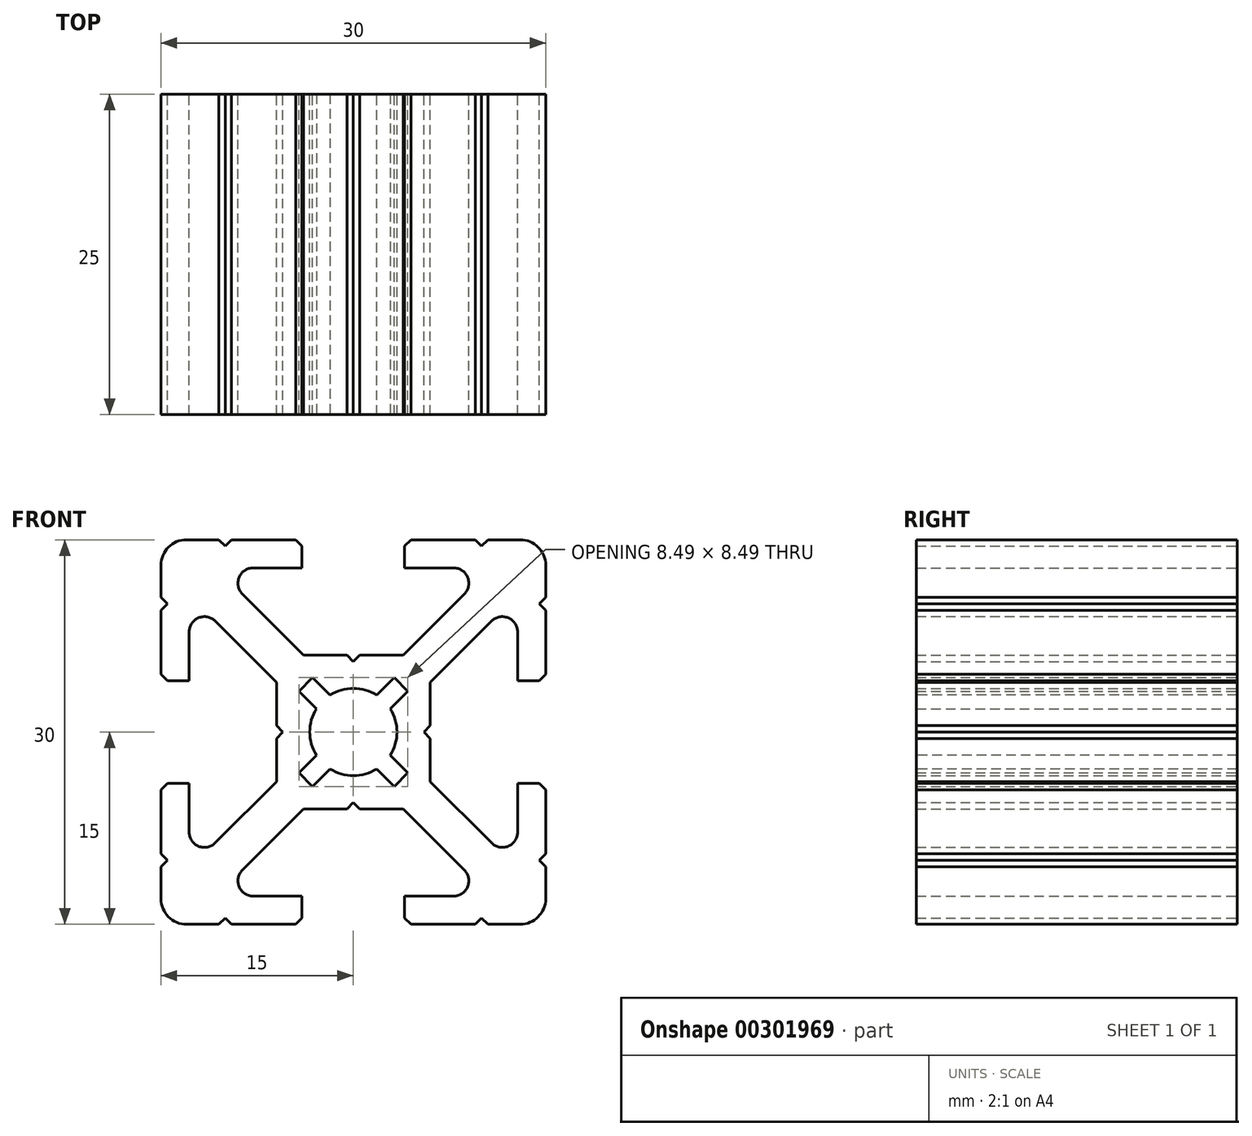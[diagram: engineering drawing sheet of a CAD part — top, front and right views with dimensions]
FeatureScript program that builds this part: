
annotation { "Feature Type Name" : "Feature", "Feature Type Description" : "" }
export const myFeature = defineFeature(function(context is Context, id is Id, definition is map)
    precondition{}
    {
        {
            var Q0;
            Q0=qCreatedBy(makeId("Front.planeOp"),FACE);
            var sketch = newSketch(context, id + "F0", { "sketchPlane" : qUnion([Q0])});
            skLineSegment(sketch, "E0", {"start": v(-2.88, -1.81) * mm, "end": v(-4.24, -3.18) * mm});
            skLineSegment(sketch, "E1", {"start": v(-4.24, -3.18) * mm, "end": v(-3.18, -4.24) * mm});
            skLineSegment(sketch, "E2", {"start": v(-3.18, -4.24) * mm, "end": v(-1.81, -2.88) * mm});
            skLineSegment(sketch, "E3", {"start": v(-1.81, -2.88) * mm, "end": v(-1.81, -2.88) * mm});
            skArc(sketch, "E4", {"start": v(-1.81, -2.88) * mm, "mid": v(0, -3.4) * mm, "end": v(1.81, -2.88) * mm});
            skLineSegment(sketch, "E5", {"start": v(1.81, -2.88) * mm, "end": v(1.81, -2.88) * mm});
            skLineSegment(sketch, "E6", {"start": v(1.81, -2.88) * mm, "end": v(3.18, -4.24) * mm});
            skLineSegment(sketch, "E7", {"start": v(3.18, -4.24) * mm, "end": v(4.24, -3.18) * mm});
            skLineSegment(sketch, "E8", {"start": v(4.24, -3.18) * mm, "end": v(2.88, -1.81) * mm});
            skLineSegment(sketch, "E9", {"start": v(2.88, -1.81) * mm, "end": v(2.88, -1.81) * mm});
            skArc(sketch, "E10", {"start": v(2.88, -1.81) * mm, "mid": v(3.4, 0) * mm, "end": v(2.88, 1.81) * mm});
            skLineSegment(sketch, "E11", {"start": v(2.88, 1.81) * mm, "end": v(2.88, 1.81) * mm});
            skLineSegment(sketch, "E12", {"start": v(2.88, 1.81) * mm, "end": v(4.24, 3.18) * mm});
            skLineSegment(sketch, "E13", {"start": v(4.24, 3.18) * mm, "end": v(3.18, 4.24) * mm});
            skLineSegment(sketch, "E14", {"start": v(3.18, 4.24) * mm, "end": v(1.81, 2.88) * mm});
            skLineSegment(sketch, "E15", {"start": v(1.81, 2.88) * mm, "end": v(1.81, 2.88) * mm});
            skArc(sketch, "E16", {"start": v(1.81, 2.88) * mm, "mid": v(0, 3.4) * mm, "end": v(-1.81, 2.88) * mm});
            skLineSegment(sketch, "E17", {"start": v(-1.81, 2.88) * mm, "end": v(-1.81, 2.88) * mm});
            skLineSegment(sketch, "E18", {"start": v(-1.81, 2.88) * mm, "end": v(-3.18, 4.24) * mm});
            skLineSegment(sketch, "E19", {"start": v(-3.18, 4.24) * mm, "end": v(-4.24, 3.18) * mm});
            skLineSegment(sketch, "E20", {"start": v(-4.24, 3.18) * mm, "end": v(-2.88, 1.81) * mm});
            skLineSegment(sketch, "E21", {"start": v(-2.88, 1.81) * mm, "end": v(-2.88, 1.81) * mm});
            skArc(sketch, "E22", {"start": v(-2.88, 1.81) * mm, "mid": v(-3.4, 0) * mm, "end": v(-2.88, -1.81) * mm});
            skArc(sketch, "E23", {"start": v(-10.77, 8.65) * mm, "mid": v(-11.38, 8.98) * mm, "end": v(-12.07, 8.9) * mm});
            skArc(sketch, "E24", {"start": v(-12.07, 8.9) * mm, "mid": v(-12.6, 8.47) * mm, "end": v(-12.8, 7.81) * mm});
            skLineSegment(sketch, "E25", {"start": v(-12.8, 7.81) * mm, "end": v(-12.8, 4) * mm});
            skLineSegment(sketch, "E26", {"start": v(-12.8, 4) * mm, "end": v(-14.5, 4) * mm});
            skLineSegment(sketch, "E27", {"start": v(-14.5, 4) * mm, "end": v(-15, 4.5) * mm});
            skLineSegment(sketch, "E28", {"start": v(-15, 4.5) * mm, "end": v(-15, 9.5) * mm});
            skLineSegment(sketch, "E29", {"start": v(-15, 9.5) * mm, "end": v(-14.5, 10) * mm});
            skLineSegment(sketch, "E30", {"start": v(-14.5, 10) * mm, "end": v(-15, 10.5) * mm});
            skLineSegment(sketch, "E31", {"start": v(-15, 10.5) * mm, "end": v(-15, 13) * mm});
            skLineSegment(sketch, "E32", {"start": v(-15, 13) * mm, "end": v(-15, 13) * mm});
            skArc(sketch, "E33", {"start": v(-13, 15) * mm, "mid": v(-14.41, 14.41) * mm, "end": v(-15, 13) * mm});
            skLineSegment(sketch, "E34", {"start": v(-13, 15) * mm, "end": v(-13, 15) * mm});
            skLineSegment(sketch, "E35", {"start": v(-13, 15) * mm, "end": v(-10.5, 15) * mm});
            skLineSegment(sketch, "E36", {"start": v(-10.5, 15) * mm, "end": v(-10, 14.5) * mm});
            skLineSegment(sketch, "E37", {"start": v(-10, 14.5) * mm, "end": v(-9.5, 15) * mm});
            skLineSegment(sketch, "E38", {"start": v(-9.5, 15) * mm, "end": v(-4.5, 15) * mm});
            skLineSegment(sketch, "E39", {"start": v(-4.5, 15) * mm, "end": v(-4, 14.5) * mm});
            skLineSegment(sketch, "E40", {"start": v(-4, 14.5) * mm, "end": v(-4, 12.8) * mm});
            skLineSegment(sketch, "E41", {"start": v(-4, 12.8) * mm, "end": v(-7.81, 12.8) * mm});
            skArc(sketch, "E42", {"start": v(-7.81, 12.8) * mm, "mid": v(-8.47, 12.6) * mm, "end": v(-8.9, 12.07) * mm});
            skArc(sketch, "E43", {"start": v(-8.9, 12.07) * mm, "mid": v(-8.98, 11.38) * mm, "end": v(-8.65, 10.77) * mm});
            skLineSegment(sketch, "E44", {"start": v(-8.65, 10.77) * mm, "end": v(-3.88, 6) * mm});
            skLineSegment(sketch, "E45", {"start": v(-3.88, 6) * mm, "end": v(-0.5, 6) * mm});
            skLineSegment(sketch, "E46", {"start": v(-0.5, 6) * mm, "end": v(0, 5.5) * mm});
            skLineSegment(sketch, "E47", {"start": v(0, 5.5) * mm, "end": v(0.5, 6) * mm});
            skLineSegment(sketch, "E48", {"start": v(0.5, 6) * mm, "end": v(3.88, 6) * mm});
            skLineSegment(sketch, "E49", {"start": v(3.88, 6) * mm, "end": v(8.65, 10.77) * mm});
            skArc(sketch, "E50", {"start": v(8.65, 10.77) * mm, "mid": v(8.98, 11.38) * mm, "end": v(8.9, 12.07) * mm});
            skArc(sketch, "E51", {"start": v(8.9, 12.07) * mm, "mid": v(8.47, 12.6) * mm, "end": v(7.81, 12.8) * mm});
            skLineSegment(sketch, "E52", {"start": v(7.81, 12.8) * mm, "end": v(4, 12.8) * mm});
            skLineSegment(sketch, "E53", {"start": v(4, 12.8) * mm, "end": v(4, 14.5) * mm});
            skLineSegment(sketch, "E54", {"start": v(4, 14.5) * mm, "end": v(4.5, 15) * mm});
            skLineSegment(sketch, "E55", {"start": v(4.5, 15) * mm, "end": v(9.5, 15) * mm});
            skLineSegment(sketch, "E56", {"start": v(9.5, 15) * mm, "end": v(10, 14.5) * mm});
            skLineSegment(sketch, "E57", {"start": v(10, 14.5) * mm, "end": v(10.5, 15) * mm});
            skLineSegment(sketch, "E58", {"start": v(10.5, 15) * mm, "end": v(13, 15) * mm});
            skLineSegment(sketch, "E59", {"start": v(13, 15) * mm, "end": v(13, 15) * mm});
            skArc(sketch, "E60", {"start": v(15, 13) * mm, "mid": v(14.41, 14.41) * mm, "end": v(13, 15) * mm});
            skLineSegment(sketch, "E61", {"start": v(15, 13) * mm, "end": v(15, 13) * mm});
            skLineSegment(sketch, "E62", {"start": v(15, 13) * mm, "end": v(15, 10.5) * mm});
            skLineSegment(sketch, "E63", {"start": v(15, 10.5) * mm, "end": v(14.5, 10) * mm});
            skLineSegment(sketch, "E64", {"start": v(14.5, 10) * mm, "end": v(15, 9.5) * mm});
            skLineSegment(sketch, "E65", {"start": v(15, 9.5) * mm, "end": v(15, 4.5) * mm});
            skLineSegment(sketch, "E66", {"start": v(15, 4.5) * mm, "end": v(14.5, 4) * mm});
            skLineSegment(sketch, "E67", {"start": v(14.5, 4) * mm, "end": v(12.8, 4) * mm});
            skLineSegment(sketch, "E68", {"start": v(12.8, 4) * mm, "end": v(12.8, 7.81) * mm});
            skArc(sketch, "E69", {"start": v(12.8, 7.81) * mm, "mid": v(12.6, 8.47) * mm, "end": v(12.07, 8.9) * mm});
            skArc(sketch, "E70", {"start": v(12.07, 8.9) * mm, "mid": v(11.38, 8.98) * mm, "end": v(10.77, 8.65) * mm});
            skLineSegment(sketch, "E71", {"start": v(10.77, 8.65) * mm, "end": v(10.77, 8.65) * mm});
            skLineSegment(sketch, "E72", {"start": v(10.77, 8.65) * mm, "end": v(6, 3.88) * mm});
            skLineSegment(sketch, "E73", {"start": v(6, 3.88) * mm, "end": v(6, 0.5) * mm});
            skLineSegment(sketch, "E74", {"start": v(6, 0.5) * mm, "end": v(5.5, 0) * mm});
            skLineSegment(sketch, "E75", {"start": v(5.5, 0) * mm, "end": v(6, -0.5) * mm});
            skLineSegment(sketch, "E76", {"start": v(6, -0.5) * mm, "end": v(6, -3.88) * mm});
            skLineSegment(sketch, "E77", {"start": v(6, -3.88) * mm, "end": v(10.77, -8.65) * mm});
            skLineSegment(sketch, "E78", {"start": v(10.77, -8.65) * mm, "end": v(10.77, -8.65) * mm});
            skArc(sketch, "E79", {"start": v(10.77, -8.65) * mm, "mid": v(11.38, -8.98) * mm, "end": v(12.07, -8.9) * mm});
            skArc(sketch, "E80", {"start": v(12.07, -8.9) * mm, "mid": v(12.6, -8.47) * mm, "end": v(12.8, -7.81) * mm});
            skLineSegment(sketch, "E81", {"start": v(12.8, -7.81) * mm, "end": v(12.8, -4) * mm});
            skLineSegment(sketch, "E82", {"start": v(12.8, -4) * mm, "end": v(14.5, -4) * mm});
            skLineSegment(sketch, "E83", {"start": v(14.5, -4) * mm, "end": v(15, -4.5) * mm});
            skLineSegment(sketch, "E84", {"start": v(15, -4.5) * mm, "end": v(15, -9.5) * mm});
            skLineSegment(sketch, "E85", {"start": v(15, -9.5) * mm, "end": v(14.5, -10) * mm});
            skLineSegment(sketch, "E86", {"start": v(14.5, -10) * mm, "end": v(15, -10.5) * mm});
            skLineSegment(sketch, "E87", {"start": v(15, -10.5) * mm, "end": v(15, -13) * mm});
            skLineSegment(sketch, "E88", {"start": v(15, -13) * mm, "end": v(15, -13) * mm});
            skArc(sketch, "E89", {"start": v(13, -15) * mm, "mid": v(14.41, -14.41) * mm, "end": v(15, -13) * mm});
            skLineSegment(sketch, "E90", {"start": v(13, -15) * mm, "end": v(13, -15) * mm});
            skLineSegment(sketch, "E91", {"start": v(13, -15) * mm, "end": v(10.5, -15) * mm});
            skLineSegment(sketch, "E92", {"start": v(10.5, -15) * mm, "end": v(10, -14.5) * mm});
            skLineSegment(sketch, "E93", {"start": v(10, -14.5) * mm, "end": v(9.5, -15) * mm});
            skLineSegment(sketch, "E94", {"start": v(9.5, -15) * mm, "end": v(4.5, -15) * mm});
            skLineSegment(sketch, "E95", {"start": v(4.5, -15) * mm, "end": v(4, -14.5) * mm});
            skLineSegment(sketch, "E96", {"start": v(4, -14.5) * mm, "end": v(4, -12.8) * mm});
            skLineSegment(sketch, "E97", {"start": v(4, -12.8) * mm, "end": v(7.81, -12.8) * mm});
            skArc(sketch, "E98", {"start": v(7.81, -12.8) * mm, "mid": v(8.47, -12.6) * mm, "end": v(8.9, -12.07) * mm});
            skArc(sketch, "E99", {"start": v(8.9, -12.07) * mm, "mid": v(8.98, -11.38) * mm, "end": v(8.65, -10.77) * mm});
            skLineSegment(sketch, "E100", {"start": v(8.65, -10.77) * mm, "end": v(3.88, -6) * mm});
            skLineSegment(sketch, "E101", {"start": v(3.88, -6) * mm, "end": v(0.5, -6) * mm});
            skLineSegment(sketch, "E102", {"start": v(0.5, -6) * mm, "end": v(0, -5.5) * mm});
            skLineSegment(sketch, "E103", {"start": v(0, -5.5) * mm, "end": v(-0.5, -6) * mm});
            skLineSegment(sketch, "E104", {"start": v(-0.5, -6) * mm, "end": v(-3.88, -6) * mm});
            skLineSegment(sketch, "E105", {"start": v(-3.88, -6) * mm, "end": v(-8.65, -10.77) * mm});
            skArc(sketch, "E106", {"start": v(-8.65, -10.77) * mm, "mid": v(-8.98, -11.38) * mm, "end": v(-8.9, -12.07) * mm});
            skArc(sketch, "E107", {"start": v(-8.9, -12.07) * mm, "mid": v(-8.47, -12.6) * mm, "end": v(-7.81, -12.8) * mm});
            skLineSegment(sketch, "E108", {"start": v(-7.81, -12.8) * mm, "end": v(-4, -12.8) * mm});
            skLineSegment(sketch, "E109", {"start": v(-4, -12.8) * mm, "end": v(-4, -14.5) * mm});
            skLineSegment(sketch, "E110", {"start": v(-4, -14.5) * mm, "end": v(-4.5, -15) * mm});
            skLineSegment(sketch, "E111", {"start": v(-4.5, -15) * mm, "end": v(-9.5, -15) * mm});
            skLineSegment(sketch, "E112", {"start": v(-9.5, -15) * mm, "end": v(-10, -14.5) * mm});
            skLineSegment(sketch, "E113", {"start": v(-10, -14.5) * mm, "end": v(-10.5, -15) * mm});
            skLineSegment(sketch, "E114", {"start": v(-10.5, -15) * mm, "end": v(-13, -15) * mm});
            skLineSegment(sketch, "E115", {"start": v(-13, -15) * mm, "end": v(-13, -15) * mm});
            skArc(sketch, "E116", {"start": v(-15, -13) * mm, "mid": v(-14.41, -14.41) * mm, "end": v(-13, -15) * mm});
            skLineSegment(sketch, "E117", {"start": v(-15, -13) * mm, "end": v(-15, -13) * mm});
            skLineSegment(sketch, "E118", {"start": v(-15, -13) * mm, "end": v(-15, -10.5) * mm});
            skLineSegment(sketch, "E119", {"start": v(-15, -10.5) * mm, "end": v(-14.5, -10) * mm});
            skLineSegment(sketch, "E120", {"start": v(-14.5, -10) * mm, "end": v(-15, -9.5) * mm});
            skLineSegment(sketch, "E121", {"start": v(-15, -9.5) * mm, "end": v(-15, -4.5) * mm});
            skLineSegment(sketch, "E122", {"start": v(-15, -4.5) * mm, "end": v(-14.5, -4) * mm});
            skLineSegment(sketch, "E123", {"start": v(-14.5, -4) * mm, "end": v(-12.8, -4) * mm});
            skLineSegment(sketch, "E124", {"start": v(-12.8, -4) * mm, "end": v(-12.8, -7.81) * mm});
            skArc(sketch, "E125", {"start": v(-12.8, -7.81) * mm, "mid": v(-12.6, -8.47) * mm, "end": v(-12.07, -8.9) * mm});
            skArc(sketch, "E126", {"start": v(-12.07, -8.9) * mm, "mid": v(-11.38, -8.98) * mm, "end": v(-10.77, -8.65) * mm});
            skLineSegment(sketch, "E127", {"start": v(-10.77, -8.65) * mm, "end": v(-10.77, -8.65) * mm});
            skLineSegment(sketch, "E128", {"start": v(-10.77, -8.65) * mm, "end": v(-6, -3.88) * mm});
            skLineSegment(sketch, "E129", {"start": v(-6, -3.88) * mm, "end": v(-6, -0.5) * mm});
            skLineSegment(sketch, "E130", {"start": v(-6, -0.5) * mm, "end": v(-5.5, 0) * mm});
            skLineSegment(sketch, "E131", {"start": v(-5.5, 0) * mm, "end": v(-6, 0.5) * mm});
            skLineSegment(sketch, "E132", {"start": v(-6, 0.5) * mm, "end": v(-6, 3.88) * mm});
            skLineSegment(sketch, "E133", {"start": v(-6, 3.88) * mm, "end": v(-10.77, 8.65) * mm});
            skSolve(sketch);
        }
        {
            var Q0;
            Q0=makeQuery(id+"F0.imprint","IMPRINT",FACE,{"disambiguationData":[TD([[makeQuery(id+"F0.imprint","IMPRINT",EDGE,{"derivedFrom":sQuery(id+"F0.wireOp",EDGE,"E0")}),-1.0]])]});
            extrude(context, id + "F1", {"entities" : qUnion([Q0]), "depth" : 25 * mm});
        }
    });
